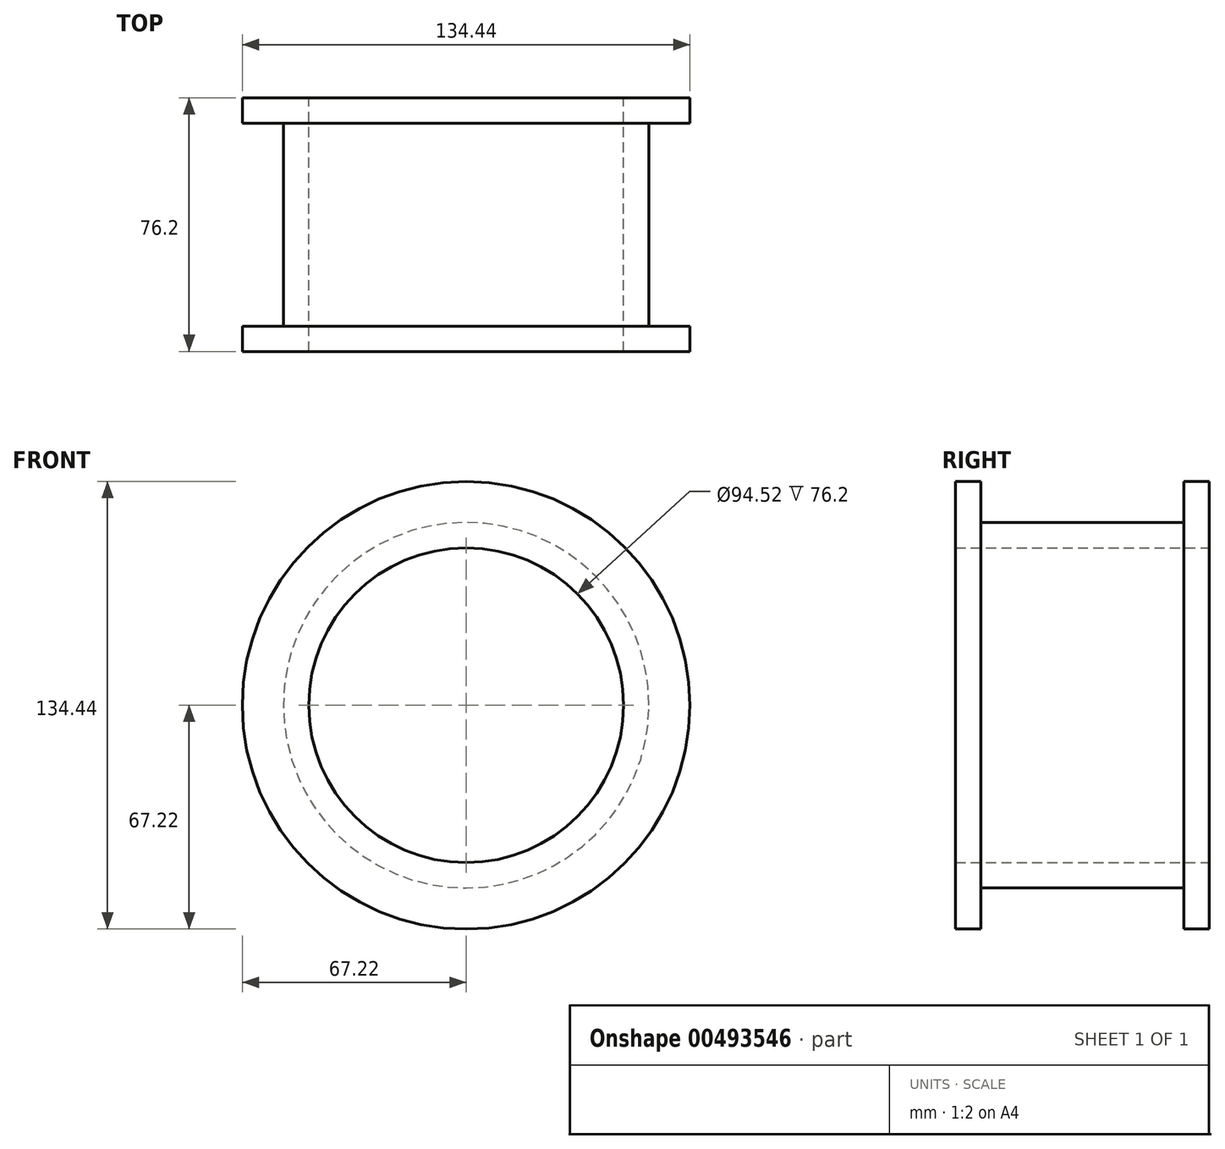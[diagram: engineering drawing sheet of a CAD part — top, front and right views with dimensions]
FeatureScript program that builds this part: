
annotation { "Feature Type Name" : "Feature", "Feature Type Description" : "" }
export const myFeature = defineFeature(function(context is Context, id is Id, definition is map)
    precondition{}
    {
        {
            var Q0;
            Q0=qCreatedBy(makeId("Front.planeOp"),FACE);
            var sketch = newSketch(context, id + "F0", { "sketchPlane" : qUnion([Q0])});
            skCircle(sketch, "E0", {"center": v(0, 0) * mm, "radius": 47.26 * mm});
            skCircle(sketch, "E1", {"center": v(0, 0) * mm, "radius": 67.22 * mm});
            skSolve(sketch);
        }
        {
            var Q0;
            Q0 = qSketchRegion(id + "F0", true);
            extrude(context, id + "F1", {"entities" : qUnion([Q0]), "depth" : 76.2 * mm});
        }
        {
            var Q0;
            Q0=makeQuery(id+"F1.opExtrude","SWEPT_FACE",FACE,{"disambiguationData":[OSD([sQuery(id+"F0.wireOp",EDGE,"E1")])]});
            shell(context, id + "F2", {"entities" : qUnion([Q0]), "thickness" : 7.62 * mm});
        }
    });
